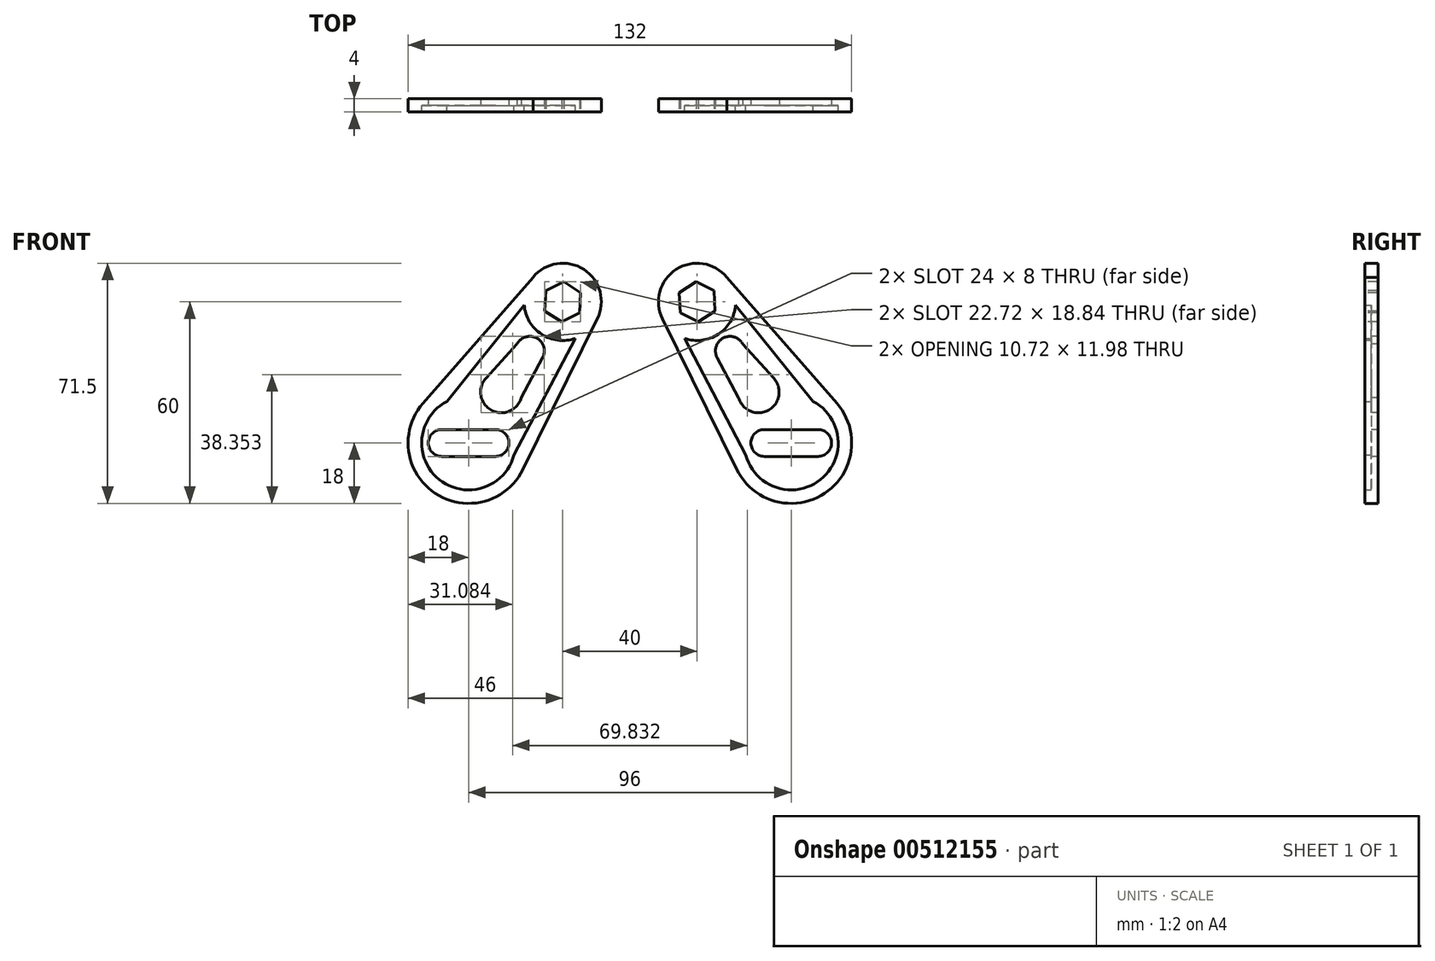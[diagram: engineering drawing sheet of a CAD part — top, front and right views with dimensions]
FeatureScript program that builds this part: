
annotation { "Feature Type Name" : "Feature", "Feature Type Description" : "" }
export const myFeature = defineFeature(function(context is Context, id is Id, definition is map)
    precondition{}
    {
        {
            var Q0;
            Q0=qCreatedBy(makeId("Front.planeOp"),FACE);
            var sketch = newSketch(context, id + "F0", { "sketchPlane" : qUnion([Q0])});
            skCircle(sketch, "E0", {"center": v(-20, 60) * mm, "radius": 11.5 * mm});
            skCircle(sketch, "E1.cCircle", {"center": v(-20, 60) * mm, "radius": 6 * mm, "construction": true});
            skLineSegment(sketch, "E1.0", {"start": v(-19.65, 66) * mm, "end": v(-14.64, 62.7) * mm});
            skLineSegment(sketch, "E1.1", {"start": v(-14.64, 62.7) * mm, "end": v(-14.99, 56.7) * mm});
            skLineSegment(sketch, "E1.2", {"start": v(-14.99, 56.7) * mm, "end": v(-20.35, 54) * mm});
            skLineSegment(sketch, "E1.3", {"start": v(-20.35, 54) * mm, "end": v(-25.36, 57.3) * mm});
            skLineSegment(sketch, "E1.4", {"start": v(-25.36, 57.3) * mm, "end": v(-25.01, 63.3) * mm});
            skLineSegment(sketch, "E1.5", {"start": v(-25.01, 63.3) * mm, "end": v(-19.65, 66) * mm});
            skCircle(sketch, "E2", {"center": v(-48, 18) * mm, "radius": 4 * mm});
            skCircle(sketch, "E3", {"center": v(-48, 18) * mm, "radius": 18 * mm});
            skLineSegment(sketch, "E4", {"start": v(-28.85, 67.34) * mm, "end": v(-62.41, 28.86) * mm});
            skLineSegment(sketch, "E5", {"start": v(-9.69, 54.9) * mm, "end": v(-31.82, 10.11) * mm});
            skCircle(sketch, "E6", {"center": v(-29.78, 45.43) * mm, "radius": 4.3 * mm});
            skCircle(sketch, "E7", {"center": v(-38.26, 33.14) * mm, "radius": 6.16 * mm});
            skLineSegment(sketch, "E8", {"start": v(-42.82, 37.28) * mm, "end": v(-33.58, 47.44) * mm});
            skLineSegment(sketch, "E9", {"start": v(-32.34, 31.45) * mm, "end": v(-25.98, 43.41) * mm});
            skLineSegment(sketch, "E10.bottom", {"start": v(-40, 22) * mm, "end": v(-56, 22) * mm});
            skLineSegment(sketch, "E10.top", {"start": v(-40, 14) * mm, "end": v(-56, 14) * mm});
            skLineSegment(sketch, "E10.left", {"start": v(-40, 22) * mm, "end": v(-40, 14) * mm});
            skLineSegment(sketch, "E10.right", {"start": v(-56, 22) * mm, "end": v(-56, 14) * mm});
            skCircle(sketch, "E11", {"center": v(-40, 18) * mm, "radius": 4 * mm});
            skCircle(sketch, "E12", {"center": v(-56, 18) * mm, "radius": 4 * mm});
            skCircle(sketch, "E13", {"center": v(-20, 60) * mm, "radius": 6.75 * mm});
            skSolve(sketch);
        }
        {
            var Q0;
            {var subQ4=sQuery(id+"F0.wireOp",EDGE,"E8");Q0=makeQuery(id+"F0.imprint","IMPRINT",FACE,{"disambiguationData":[TD([[makeQuery(id+"F0.imprint","IMPRINT",EDGE,{"derivedFrom":subQ4}),1.0]])]});}
            var Q1;
            Q1=makeQuery(id+"F0.imprint","IMPRINT",FACE,{"disambiguationData":[TD([[makeQuery(id+"F0.imprint","IMPRINT",EDGE,{"derivedFrom":sQuery(id+"F0.wireOp",EDGE,"E1.0")}),1.0]])]});
            var Q2;
            {var subQ0=sQuery(id+"F0.wireOp",EDGE,"E5");var subQ1=sQuery(id+"F0.wireOp",EDGE,"E0");var subQ2=makeQuery(id+"F0.imprint","INTERSECT",VERTEX,{"derivedFrom":[subQ1,subQ0]});Q2=makeQuery(id+"F0.imprint","IMPRINT",FACE,{"disambiguationData":[TD([[makeQuery(id+"F0.imprint","IMPRINT",EDGE,{"disambiguationData":[TD([[subQ2,1.0]])],"derivedFrom":subQ1}),-1.0]])]});}
            var Q3;
            {var subQ0=sQuery(id+"F0.wireOp",EDGE,"E3");var subQ5=makeQuery(id+"F0.imprint","INTERSECT",VERTEX,{"derivedFrom":[subQ0,sQuery(id+"F0.wireOp",EDGE,"E4")]});Q3=makeQuery(id+"F0.imprint","IMPRINT",FACE,{"disambiguationData":[TD([[makeQuery(id+"F0.imprint","IMPRINT",EDGE,{"disambiguationData":[TD([[subQ5,1.0]])],"derivedFrom":subQ0}),1.0]])]});}
            var Q4;
            Q4=makeQuery(id+"F0.imprint","IMPRINT",FACE,{"disambiguationData":[TD([[makeQuery(id+"F0.imprint","IMPRINT",EDGE,{"derivedFrom":sQuery(id+"F0.wireOp",EDGE,"E13")}),-1.0]])]});
            var Q5;
            {var subQ17=sQuery(id+"F0.wireOp",EDGE,"E6JxvTyD-7h0c-zLrh-W3ln-XbGqjIQrVXuG");Q5=makeQuery(id+"F0.imprint","IMPRINT",FACE,{"disambiguationData":[TD([[makeQuery(id+"F0.imprint","IMPRINT",EDGE,{"derivedFrom":subQ17}),-1.0]])]});}
            extrude(context, id + "F1", {"entities" : qUnion([Q0, Q1, Q2, Q3, Q4, Q5]), "flatOperationType" : FlatOperationType.REMOVE, "oppositeDirection" : true, "depth" : 2 * mm, "offsetDistance" : 25 * mm, "domain" : OperationDomain.MODEL});
        }
        {
            var Q0;
            Q0=makeQuery(id+"F0.imprint","IMPRINT",FACE,{"disambiguationData":[TD([[makeQuery(id+"F0.imprint","IMPRINT",EDGE,{"derivedFrom":sQuery(id+"F0.wireOp",EDGE,"E1.0")}),1.0]])]});
            var Q1;
            Q1=makeQuery(id+"F0.imprint","IMPRINT",FACE,{"disambiguationData":[TD([[makeQuery(id+"F0.imprint","IMPRINT",EDGE,{"derivedFrom":sQuery(id+"F0.wireOp",EDGE,"E13")}),-1.0]])]});
            extrude(context, id + "F2", {"entities" : qUnion([Q0, Q1]), "operationType" : NewBodyOperationType.ADD, "flatOperationType" : FlatOperationType.REMOVE, "depth" : 2 * mm, "offsetDistance" : 25 * mm, "domain" : OperationDomain.MODEL});
        }
        {
            var Q0;
            {var subQ1=sQuery(id+"F0.wireOp",EDGE,"E3");var subQ5=makeQuery(id+"F0.imprint","INTERSECT",VERTEX,{"derivedFrom":[subQ1,sQuery(id+"F0.wireOp",EDGE,"E4")]});Q0=makeQuery(id+"F0.imprint","IMPRINT",FACE,{"disambiguationData":[TD([[makeQuery(id+"F0.imprint","IMPRINT",EDGE,{"disambiguationData":[TD([[subQ5,1.0]])],"derivedFrom":subQ1}),1.0]])]});}
            var sketch = newSketch(context, id + "F3", { "sketchPlane" : qUnion([Q0])});
            skCircle(sketch, "E14", {"center": v(-48, 18) * mm, "radius": 13.98 * mm});
            skLineSegment(sketch, "E15", {"start": v(-54.5, 30.38) * mm, "end": v(-30.15, 60.7) * mm});
            skLineSegment(sketch, "E16", {"start": v(-30.15, 60.7) * mm, "end": v(-25.88, 50.92) * mm});
            skLineSegment(sketch, "E17", {"start": v(-25.88, 50.92) * mm, "end": v(-15.28, 50.92) * mm});
            skLineSegment(sketch, "E18", {"start": v(-15.28, 50.92) * mm, "end": v(-34.5, 14.4) * mm});
            skLineSegment(sketch, "E19.0", {"start": v(-28.85, 67.34) * mm, "end": v(-62.41, 28.86) * mm});
            skCircle(sketch, "E20.0", {"center": v(-48, 18) * mm, "radius": 18 * mm});
            skLineSegment(sketch, "E21.0", {"start": v(-9.69, 54.9) * mm, "end": v(-31.82, 10.11) * mm});
            skCircle(sketch, "E22.0", {"center": v(-20, 60) * mm, "radius": 11.5 * mm});
            skSolve(sketch);
        }
        {
            var Q0;
            {var subQ5=sQuery(id+"F3.wireOp",EDGE,"E21.0");Q0=makeQuery(id+"F3.imprint","IMPRINT",FACE,{"disambiguationData":[TD([[makeQuery(id+"F3.imprint","IMPRINT",EDGE,{"derivedFrom":subQ5}),-1.0]])]});}
            var Q1;
            {var subQ2=sQuery(id+"F3.wireOp",EDGE,"E15");var subQ5=sQuery(id+"F3.wireOp",EDGE,"E14");var subQ8=makeQuery(id+"F3.imprint","INTERSECT",VERTEX,{"derivedFrom":[subQ5,subQ2]});Q1=makeQuery(id+"F3.imprint","IMPRINT",FACE,{"disambiguationData":[TD([[makeQuery(id+"F3.imprint","IMPRINT",EDGE,{"disambiguationData":[TD([[subQ8,-1.0]])],"derivedFrom":subQ5}),-1.0]])]});}
            var Q2;
            {var subQ0=sQuery(id+"F3.wireOp",EDGE,"E20.0");var subQ1=sQuery(id+"F3.wireOp",EDGE,"E15");var subQ2=makeQuery(id+"F3.imprint","INTERSECT",VERTEX,{"derivedFrom":[subQ1,subQ0]});Q2=makeQuery(id+"F3.imprint","IMPRINT",FACE,{"disambiguationData":[TD([[makeQuery(id+"F3.imprint","IMPRINT",EDGE,{"disambiguationData":[TD([[subQ2,-1.0]])],"derivedFrom":subQ1}),1.0]])]});}
            extrude(context, id + "F4", {"entities" : qUnion([Q0, Q1, Q2]), "operationType" : NewBodyOperationType.ADD, "flatOperationType" : FlatOperationType.REMOVE, "depth" : 2 * mm, "offsetDistance" : 25 * mm, "domain" : OperationDomain.MODEL});
        }
        {
            var Q0;
            Q0=makeQuery(id+"F1.opExtrude","SWEPT_BODY",BODY,{"disambiguationData":[OSD([sQuery(id+"F0.wireOp",EDGE,"E0"),sQuery(id+"F0.wireOp",EDGE,"E1.0"),sQuery(id+"F0.wireOp",EDGE,"E1.1"),sQuery(id+"F0.wireOp",EDGE,"E1.2"),sQuery(id+"F0.wireOp",EDGE,"E1.3"),sQuery(id+"F0.wireOp",EDGE,"E1.4"),sQuery(id+"F0.wireOp",EDGE,"E1.5"),sQuery(id+"F0.wireOp",EDGE,"E3"),sQuery(id+"F0.wireOp",EDGE,"E4"),sQuery(id+"F0.wireOp",EDGE,"E5"),sQuery(id+"F0.wireOp",EDGE,"ygmoQ5Yp-AUWN-CLWn-WjGI-evySKiIfosqw"),sQuery(id+"F0.wireOp",EDGE,"E6JxvTyD-7h0c-zLrh-W3ln-XbGqjIQrVXuG"),sQuery(id+"F0.wireOp",EDGE,"E6"),sQuery(id+"F0.wireOp",EDGE,"E7"),sQuery(id+"F0.wireOp",EDGE,"0qzaO05h-A5VA-jcvg-QrVN-jCnUtnLoAO9P"),sQuery(id+"F0.wireOp",EDGE,"Xfnr7tYI-IueN-FQoz-P70B-6cQvtyO5KWsr"),sQuery(id+"F0.wireOp",EDGE,"rvoj9FYf-gdXb-EvWC-HlZd-O0gizpXoAeAQ"),sQuery(id+"F0.wireOp",EDGE,"TEg4JBBB-ZK13-8ir8-ZAA9-4v1OzwWhPDci"),sQuery(id+"F0.wireOp",EDGE,"2CCBNNSq-gF74-TTZi-XyDB-a3Y81bialhqU"),sQuery(id+"F0.wireOp",EDGE,"wjZYrWHo-NbOR-1QJi-kguJ-2v9ZDjugmpZ9"),sQuery(id+"F0.wireOp",EDGE,"uh4LWXup-hHFa-LFph-I8Sa-qQj7mYBBZZzC"),sQuery(id+"F0.wireOp",EDGE,"emCSmVxo-lETy-yOrQ-GncP-KLNIzIKa9T1W"),sQuery(id+"F0.wireOp",EDGE,"6VTC22w7-9teT-RS0k-EVhR-HYNZWubJiTpv"),sQuery(id+"F0.wireOp",EDGE,"E8"),sQuery(id+"F0.wireOp",EDGE,"E9"),sQuery(id+"F0.wireOp",EDGE,"E10.bottom"),sQuery(id+"F0.wireOp",EDGE,"E10.top"),sQuery(id+"F0.wireOp",EDGE,"E11"),sQuery(id+"F0.wireOp",EDGE,"E12"),sQuery(id+"F0.wireOp",EDGE,"gI9HPeNz-oTQU-kQO2-MRxQ-E0rnYhTAeuEL"),sQuery(id+"F0.wireOp",EDGE,"3oQCsyE5-13nW-6J6f-9lq5-U6Ye5FKYQ578"),sQuery(id+"F0.wireOp",EDGE,"1PZKcXJK-kqIG-lRsA-WlX7-AcK8F5797vQv"),sQuery(id+"F0.wireOp",EDGE,"mzJ3TSbc-XGWi-Kozu-LUzN-GNbCCBoXsWR1")])]});
            var Q1;
            Q1=qCreatedBy(makeId("Right.planeOp"),FACE);
            mirror(context, id + "F5", {"operationType" : NewBodyOperationType.ADD, "entities" : qUnion([Q0]), "mirrorPlane" : qUnion([Q1])});
        }
    });
